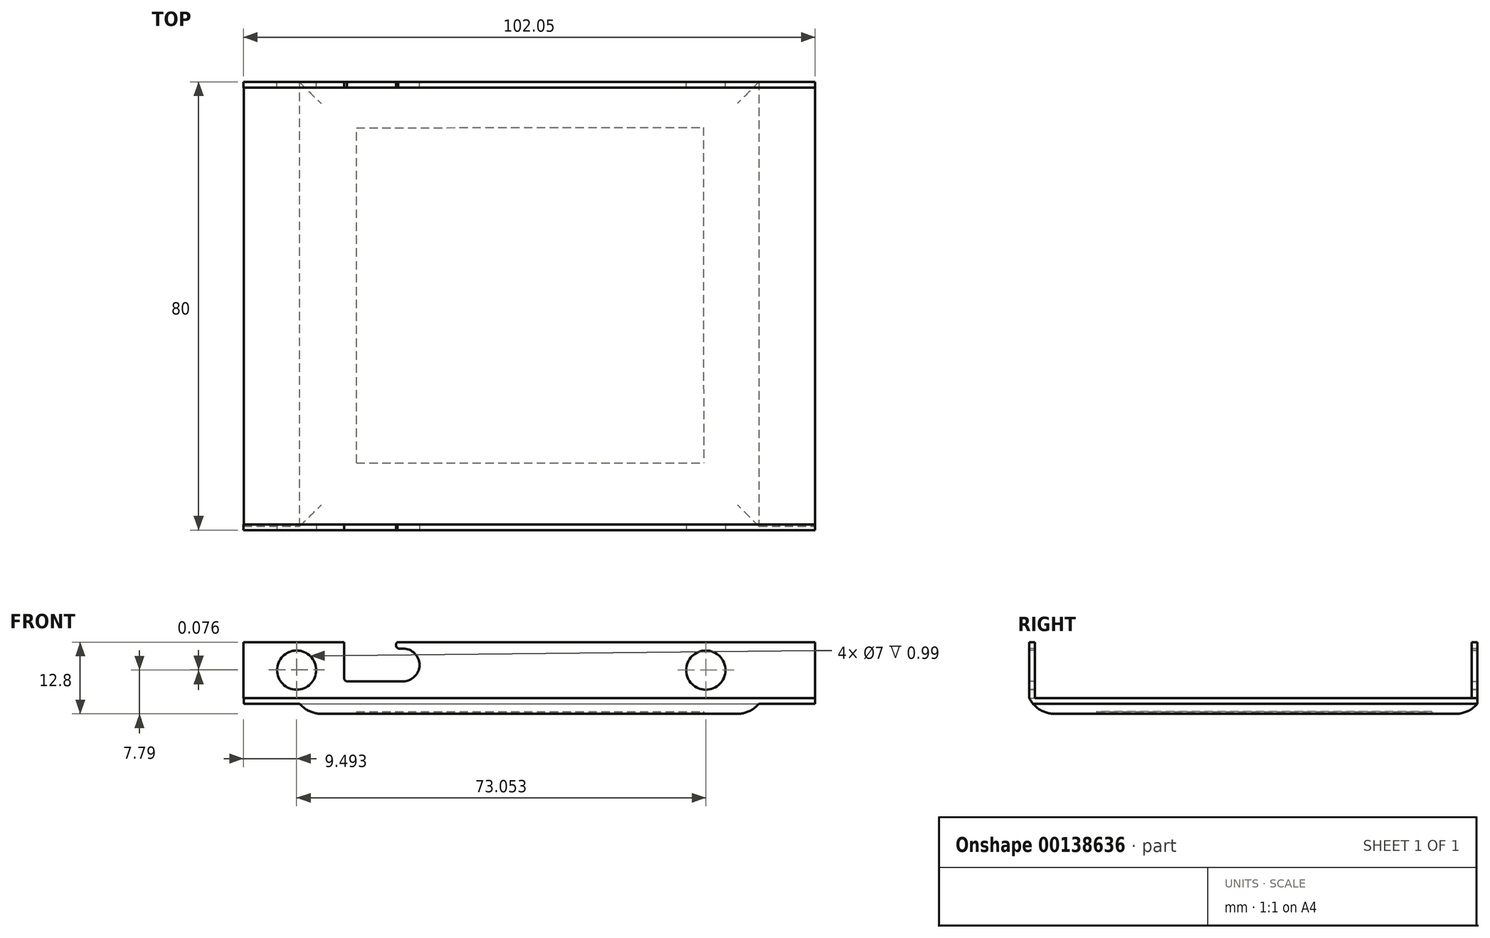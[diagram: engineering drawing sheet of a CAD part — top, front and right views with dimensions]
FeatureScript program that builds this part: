
annotation { "Feature Type Name" : "Feature", "Feature Type Description" : "" }
export const myFeature = defineFeature(function(context is Context, id is Id, definition is map)
    precondition{}
    {
        {
            var Q0;
            Q0=qCreatedBy(makeId("Top.planeOp"),FACE);
            var sketch = newSketch(context, id + "F0", { "sketchPlane" : qUnion([Q0])});
            skLineSegment(sketch, "E0", {"start": v(-42.42, -26.63) * mm, "end": v(59.58, -26.63) * mm});
            skLineSegment(sketch, "E1", {"start": v(-42.42, -26.63) * mm, "end": v(-42.42, 53.37) * mm});
            skLineSegment(sketch, "E2", {"start": v(-42.42, 53.37) * mm, "end": v(59.58, 53.37) * mm});
            skLineSegment(sketch, "E3", {"start": v(59.58, -26.63) * mm, "end": v(59.58, 53.37) * mm});
            skSolve(sketch);
        }
        {
            var Q0;
            Q0 = qSketchRegion(id + "F0", true);
            extrude(context, id + "F1", {"entities" : qUnion([Q0]), "depth" : 1 * mm});
        }
        {
            var Q0;
            Q0=makeQuery(id+"F1.opExtrude","CAP_FACE",FACE,{"disambiguationData":[OSD([sQuery(id+"F0.wireOp",EDGE,"E0"),sQuery(id+"F0.wireOp",EDGE,"E1"),sQuery(id+"F0.wireOp",EDGE,"E2"),sQuery(id+"F0.wireOp",EDGE,"E3")])],"isStart":true});
            var sketch = newSketch(context, id + "F2", { "sketchPlane" : qUnion([Q0])});
            skLineSegment(sketch, "E4", {"start": v(-32.42, 26.63) * mm, "end": v(-32.42, -53.3) * mm});
            skLineSegment(sketch, "E5", {"start": v(-32.42, -53.3) * mm, "end": v(49.58, -53.37) * mm});
            skLineSegment(sketch, "E6", {"start": v(49.58, -53.37) * mm, "end": v(49.58, 26.63) * mm});
            skLineSegment(sketch, "E7", {"start": v(-32.42, 26.63) * mm, "end": v(49.58, 26.63) * mm});
            skSolve(sketch);
        }
        {
            var Q0;
            Q0 = qSketchRegion(id + "F2", true);
            extrude(context, id + "F3", {"entities" : qUnion([Q0]), "operationType" : NewBodyOperationType.ADD, "depth" : 1.8 * mm});
        }
        {
            var Q0;
            Q0=makeQuery(id+"F3.opExtrude","CAP_FACE",FACE,{"disambiguationData":[OSD([sQuery(id+"F2.wireOp",EDGE,"E4"),sQuery(id+"F2.wireOp",EDGE,"E5"),sQuery(id+"F2.wireOp",EDGE,"E6"),sQuery(id+"F2.wireOp",EDGE,"E7")])],"isStart":false});
            var sketch = newSketch(context, id + "F4", { "sketchPlane" : qUnion([Q0])});
            skLineSegment(sketch, "E8", {"start": v(-22.28, 14.62) * mm, "end": v(-22.28, -45.18) * mm});
            skLineSegment(sketch, "E9", {"start": v(-22.28, -45.18) * mm, "end": v(39.64, -45.23) * mm});
            skLineSegment(sketch, "E10", {"start": v(39.64, -45.23) * mm, "end": v(39.7, 14.62) * mm});
            skLineSegment(sketch, "E11", {"start": v(-22.28, 14.62) * mm, "end": v(39.7, 14.62) * mm});
            skSolve(sketch);
        }
        {
            var Q0;
            Q0 = qSketchRegion(id + "F4", true);
            extrude(context, id + "F5", {"entities" : qUnion([Q0]), "operationType" : NewBodyOperationType.REMOVE, "oppositeDirection" : true, "depth" : 0.42 * mm});
        }
        {
            var Q0;
            Q0=makeQuery(id+"F5.boolean.opBoolean","COPY",EDGE,{"derivedFrom":makeQuery(id+"F5.opExtrude","CAP_EDGE",EDGE,{"disambiguationData":[OSD([sQuery(id+"F4.wireOp",EDGE,"E11")])],"isStart":true})});
            var Q1;
            Q1=makeQuery(id+"F5.boolean.opBoolean","COPY",EDGE,{"derivedFrom":makeQuery(id+"F5.opExtrude","CAP_EDGE",EDGE,{"disambiguationData":[OSD([sQuery(id+"F4.wireOp",EDGE,"E10")])],"isStart":true})});
            var Q2;
            Q2=makeQuery(id+"F5.boolean.opBoolean","COPY",EDGE,{"derivedFrom":makeQuery(id+"F5.opExtrude","CAP_EDGE",EDGE,{"disambiguationData":[OSD([sQuery(id+"F4.wireOp",EDGE,"E8")])],"isStart":true})});
            var Q3;
            Q3=makeQuery(id+"F5.boolean.opBoolean","COPY",EDGE,{"derivedFrom":makeQuery(id+"F5.opExtrude","CAP_EDGE",EDGE,{"disambiguationData":[OSD([sQuery(id+"F4.wireOp",EDGE,"E9")])],"isStart":true})});
            var Q4;
            Q4=makeQuery(id+"F3.opExtrude","CAP_EDGE",EDGE,{"disambiguationData":[OSD([sQuery(id+"F2.wireOp",EDGE,"E6")])],"isStart":false});
            var Q5;
            Q5=makeQuery(id+"F3.opExtrude","CAP_EDGE",EDGE,{"disambiguationData":[OSD([sQuery(id+"F2.wireOp",EDGE,"E5")])],"isStart":false});
            var Q6;
            Q6=makeQuery(id+"F3.opExtrude","CAP_EDGE",EDGE,{"disambiguationData":[OSD([sQuery(id+"F2.wireOp",EDGE,"E7")])],"isStart":false});
            var Q7;
            Q7=makeQuery(id+"F3.opExtrude","CAP_EDGE",EDGE,{"disambiguationData":[OSD([sQuery(id+"F2.wireOp",EDGE,"E4")])],"isStart":false});
            fillet(context, id + "F6", {"entities" : qUnion([Q0, Q1, Q2, Q3, Q4, Q5, Q6, Q7]), "radius" : 5 * mm, "tangentPropagation" : true, "allowEdgeOverflow" : false});
        }
        {
            var Q0;
            Q0=qCreatedBy(makeId("Right.planeOp"),FACE);
            var sketch = newSketch(context, id + "F7", { "sketchPlane" : qUnion([Q0])});
            skLineSegment(sketch, "E12", {"start": v(-26.62, 1) * mm, "end": v(-26.62, 11) * mm});
            skLineSegment(sketch, "E13", {"start": v(-25.62, 1) * mm, "end": v(-25.62, 11) * mm});
            skLineSegment(sketch, "E14", {"start": v(-26.62, 1) * mm, "end": v(-25.62, 1) * mm});
            skLineSegment(sketch, "E15", {"start": v(-26.62, 11) * mm, "end": v(-25.62, 11) * mm});
            skLineSegment(sketch, "E16", {"start": v(53.34, 1) * mm, "end": v(53.34, 11) * mm});
            skLineSegment(sketch, "E17", {"start": v(53.34, 1) * mm, "end": v(52.34, 1) * mm});
            skLineSegment(sketch, "E18", {"start": v(52.34, 1) * mm, "end": v(52.34, 11) * mm});
            skLineSegment(sketch, "E19", {"start": v(52.34, 11) * mm, "end": v(53.34, 11) * mm});
            skSolve(sketch);
        }
        {
            var Q0;
            Q0 = qSketchRegion(id + "F7", true);
            extrude(context, id + "F8", {"entities" : qUnion([Q0]), "operationType" : NewBodyOperationType.ADD, "depth" : 59.6 * mm, "hasSecondDirection" : true, "secondDirectionOppositeDirection" : true, "secondDirectionDepth" : 42.46 * mm});
        }
        {
            var Q0;
            Q0=makeQuery(id+"F8.opExtrude","SWEPT_FACE",FACE,{"disambiguationData":[OSD([sQuery(id+"F7.wireOp",EDGE,"E12")])]});
            var sketch = newSketch(context, id + "F9", { "sketchPlane" : qUnion([Q0])});
            skCircle(sketch, "E20", {"center": v(-32.96, 6) * mm, "radius": 3.5 * mm});
            skSolve(sketch);
        }
        {
            var Q0;
            Q0 = qSketchRegion(id + "F9", true);
            extrude(context, id + "F10", {"entities" : qUnion([Q0]), "operationType" : NewBodyOperationType.REMOVE, "oppositeDirection" : true, "depth" : 0.99 * mm});
        }
        {
            var Q0;
            Q0=makeQuery(id+"F8.opExtrude","SWEPT_FACE",FACE,{"disambiguationData":[OSD([sQuery(id+"F7.wireOp",EDGE,"E12")])]});
            var sketch = newSketch(context, id + "F11", { "sketchPlane" : qUnion([Q0])});
            skLineSegment(sketch, "E21", {"start": v(-13.96, 4) * mm, "end": v(-23.96, 4) * mm});
            skLineSegment(sketch, "E22", {"start": v(-24.46, 4.5) * mm, "end": v(-24.46, 11) * mm});
            skPoint(sketch, "E23.visualSharp", {"position": v(-24.46, 4) * mm});
            skArc(sketch, "E23.filletArc", {"start": v(-24.46, 4.5) * mm, "mid": v(-24.32, 4.14) * mm, "end": v(-23.96, 4) * mm});
            skArc(sketch, "E24", {"start": v(-13.96, 4) * mm, "mid": v(-11.04, 6.92) * mm, "end": v(-13.96, 9.84) * mm});
            skLineSegment(sketch, "E25", {"start": v(-13.96, 9.84) * mm, "end": v(-14.61, 9.84) * mm});
            skArc(sketch, "E26", {"start": v(-14.96, 11) * mm, "mid": v(-15.21, 10.29) * mm, "end": v(-14.61, 9.84) * mm});
            skLineSegment(sketch, "E27", {"start": v(-14.96, 11) * mm, "end": v(-24.46, 11) * mm});
            skSolve(sketch);
        }
        {
            var Q0;
            Q0 = qSketchRegion(id + "F11", true);
            var Q1;
            Q1=makeQuery(id+"F8.opExtrude","SWEPT_FACE",FACE,{"disambiguationData":[OSD([sQuery(id+"F7.wireOp",EDGE,"E16")])]});
            extrude(context, id + "F12", {"entities" : qUnion([Q0]), "operationType" : NewBodyOperationType.REMOVE, "oppositeDirection" : true, "endBoundEntityFace" : qUnion([Q1]), "depth" : 77.97 * mm});
        }
        {
            var Q0;
            Q0=makeQuery(id+"F8.opExtrude","SWEPT_FACE",FACE,{"disambiguationData":[OSD([sQuery(id+"F7.wireOp",EDGE,"E16")])]});
            var sketch = newSketch(context, id + "F13", { "sketchPlane" : qUnion([Q0])});
            skLineSegment(sketch, "E28", {"start": v(24.47, 11) * mm, "end": v(24.47, 4.5) * mm});
            skArc(sketch, "E29", {"start": v(23.97, 3.99) * mm, "mid": v(24.32, 4.15) * mm, "end": v(24.47, 4.5) * mm});
            skLineSegment(sketch, "E30", {"start": v(23.97, 3.99) * mm, "end": v(13.98, 3.99) * mm});
            skArc(sketch, "E31", {"start": v(13.98, 9.88) * mm, "mid": v(11.03, 6.93) * mm, "end": v(13.98, 3.99) * mm});
            skLineSegment(sketch, "E32", {"start": v(13.98, 9.88) * mm, "end": v(14.6, 9.88) * mm});
            skArc(sketch, "E33", {"start": v(14.6, 9.88) * mm, "mid": v(15.17, 10.35) * mm, "end": v(14.84, 11) * mm});
            skLineSegment(sketch, "E34", {"start": v(24.47, 11) * mm, "end": v(14.84, 11) * mm});
            skSolve(sketch);
        }
        {
            var Q0;
            Q0 = qSketchRegion(id + "F13", true);
            extrude(context, id + "F14", {"entities" : qUnion([Q0]), "operationType" : NewBodyOperationType.REMOVE, "oppositeDirection" : true, "depth" : 25 * mm});
        }
        {
            var Q0;
            Q0=makeQuery(id+"F8.opExtrude","SWEPT_FACE",FACE,{"disambiguationData":[OSD([sQuery(id+"F7.wireOp",EDGE,"E16")])]});
            var sketch = newSketch(context, id + "F15", { "sketchPlane" : qUnion([Q0])});
            skCircle(sketch, "E35", {"center": v(32.97, 6.07) * mm, "radius": 3.5 * mm});
            skSolve(sketch);
        }
        {
            var Q0;
            Q0 = qSketchRegion(id + "F15", true);
            extrude(context, id + "F16", {"entities" : qUnion([Q0]), "operationType" : NewBodyOperationType.REMOVE, "oppositeDirection" : true, "depth" : 0.99 * mm});
        }
        {
            var Q0;
            Q0=makeQuery(id+"F8.opExtrude","SWEPT_FACE",FACE,{"disambiguationData":[OSD([sQuery(id+"F7.wireOp",EDGE,"E16")])]});
            var sketch = newSketch(context, id + "F17", { "sketchPlane" : qUnion([Q0])});
            skCircle(sketch, "E36", {"center": v(-40.09, 6) * mm, "radius": 3.5 * mm});
            skSolve(sketch);
        }
        {
            var Q0;
            Q0=makeQuery(id+"F17.imprint","IMPRINT",FACE,{"disambiguationData":[TD([[makeQuery(id+"F17.imprint","IMPRINT",EDGE,{"derivedFrom":sQuery(id+"F17.wireOp",EDGE,"E36")}),1.0]])]});
            extrude(context, id + "F18", {"entities" : qUnion([Q0]), "operationType" : NewBodyOperationType.REMOVE, "oppositeDirection" : true, "depth" : 0.99 * mm});
        }
        {
            var Q0;
            Q0=makeQuery(id+"F9.imprint","IMPRINT",FACE,{"disambiguationData":[TD([[makeQuery(id+"F9.imprint","IMPRINT",EDGE,{"derivedFrom":sQuery(id+"F9.wireOp",EDGE,"E20")}),-1.0]])]});
            var sketch = newSketch(context, id + "F19", { "sketchPlane" : qUnion([Q0])});
            skCircle(sketch, "E37", {"center": v(40.08, 5.99) * mm, "radius": 3.5 * mm});
            skSolve(sketch);
        }
        {
            var Q0;
            Q0 = qSketchRegion(id + "F19", true);
            extrude(context, id + "F20", {"entities" : qUnion([Q0]), "operationType" : NewBodyOperationType.REMOVE, "oppositeDirection" : true, "depth" : 0.99 * mm});
        }
    });
